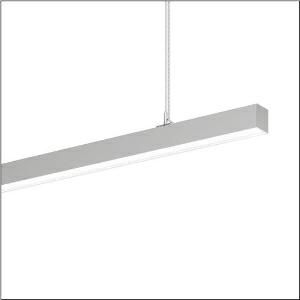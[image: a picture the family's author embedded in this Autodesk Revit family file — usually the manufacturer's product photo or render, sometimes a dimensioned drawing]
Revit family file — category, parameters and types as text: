
# Revit family: silica_r__21_51mx30tbt5s_71cb
name_source: partatom
category: Lighting Fixtures
units: mm (PartAtom-declared; Revit-internal decimal feet)

## family parameters
Cut with Voids When Loaded = No
Host = Face
Light Source = No
Part Type = Normal
Room Calculation Point = No
Round Connector Dimension = Use Diameter
Shared = No

## types (1)
- --- (1 x LED, 5150 lm, 42.2 W, 6500K)
    Apparent Load = 42 VA
    CIE Flux Codes = 47 79 96 58 100
    Color Rendering = 80
    Color Temperature = 6500K
    Default Elevation = 1800 mm
    Description = Silica® 21, office luminaire, primary optical cover: cover, of PMMA, opal, light emission: direct/indirect distribution, primary light characteristic: symmetric, installation type: suspended mounting, LED, rated luminous flux: 5.150lm, luminous efficacy: 116lm/W, light colour: 8tw, colour temperature: 2700..6500K, control gear: ECG DALI, with terminal, 3+2-pole, max. 2.5mm², mains connection: 220..240V, AC, 50/60Hz, rated input power: 44.3W, luminaire housing, of aluminium, metallic grey (RAL 9006), length: 1.504mm, width: 53mm, height: 53mm, protection rating (complete): IP20, insulation class (complete): insulation class I (protective earthing), certification: CE, permissible operating ambient temperature: 0..+35°C, standard: EN 50419, packaging unit: 1 piece
    Height = 53 mm
    Lamp = 1 x LED
    Lamp Light Flux = 5150 lm
    Lamp Power = 42.2 W
    Lamp count = 1
    Length = 1504 mm
    Luminous efficacy = 122 lm/W
    Manufacturer = Siteco
    ModVariant = No
    Model = 51MX30TBT5S
    Mounting Place = Ceiling
    Mounting Type = Pendant
    Number of Poles = 1
    OnlyDefault = Yes
    Power Factor = 1
    Product Name = Silica® 21
    Product group = office luminaire | ceiling pendant
    ProductGroupID = 902
    Protection Class = Protection class I
    Protection Degree = IP 20
    RLX_Detail_Level = 1
    RLX_Emergency_Light_Flux = 0 lm
    RLX_Emergency_Type = 0
    RLX_Emergency_Type_DB = No
    RlxData = <blob elided: 20197 chars, md5=035f19d4>
    Socket = socket
    Standby Power = 0 W
    System Light Flux = 5150 lm
    System Power = 42 W
    Type Comments = individual setting
    Type Image = l_1313621.jpg
    URL = http://relux.com
    VarID = @adj_088983
    Voltage = 0 V
    Weight = 0.00 kg
    Width = 53 mm

## geometry (parser evidence)
native form markers: Blend x4, Sweep x12
no freeform markers — native parametric forms only
